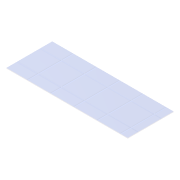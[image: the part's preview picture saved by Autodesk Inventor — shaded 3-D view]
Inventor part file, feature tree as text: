
AUTODESK INVENTOR PART (.ipt)
format: ipt  version: 2016 (Build 200138000, 138)  size: 75,264 bytes
history: native  units: mm
features: extrude x1, sketch x1
ambient origin geometry x8: Origin, YZ Plane, XZ Plane, XY Plane, X Axis, Y Axis, Z Axis, Center Point
bodies: Volumenkörper1 (feature_tree)
feature tree (2):
  extrude  "Extrusion1"  Depth=529.8mm
  sketch  "Skizze1"  dims[d0=200.0mm d1=529.8mm d2=3.0mm d3=0.0mm]
